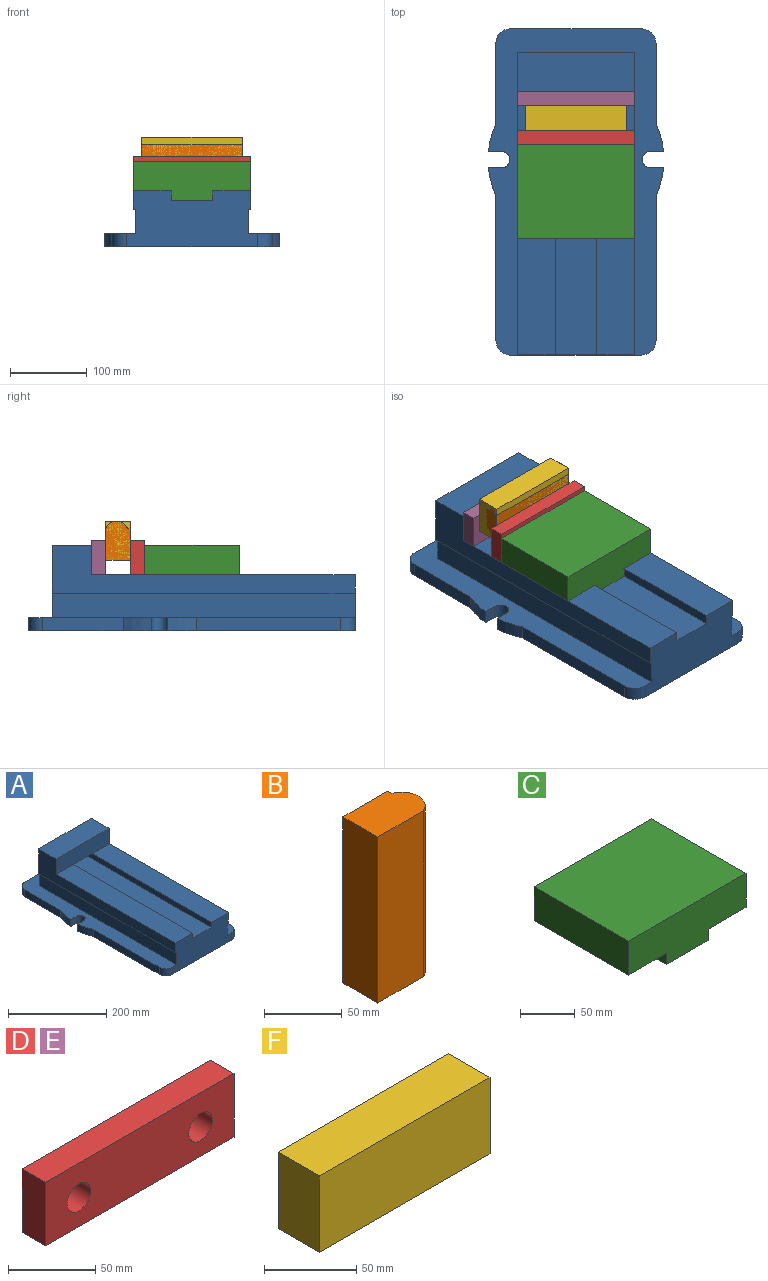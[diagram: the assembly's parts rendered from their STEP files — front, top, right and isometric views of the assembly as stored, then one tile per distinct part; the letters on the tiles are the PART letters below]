
ASSEMBLY  parts=6 mates=9
PART A: 37 faces, bbox 227.6x423.9x111.1 mm
  f0: plane 187.5x17.46mm, normal (1,0,0), area 3274.3mm2, adj f1,f18,f19,f21
  f1: cylinder r=114.3mm len=36.77mm, axis (0,0,-1), area 667.7mm2, adj f0,f2,f18,f21
  f2: plane 17.46x16.96mm, normal (0,1,0), area 296.2mm2, adj f1,f3,f18,f21
  f3: cylinder r=10.67mm len=21.35mm, axis (0,0,-1), area 585.5mm2, adj f2,f4,f18,f21
  f4: plane 17.46x16.96mm, normal (0,-1,0), area 296.2mm2, adj f3,f5,f18,f21
  f5: cylinder r=114.3mm len=36.77mm, axis (0,0,-1), area 667.7mm2, adj f4,f6,f18,f21
  f6: plane 103.37x17.46mm, normal (1,0,0), area 1805mm2, adj f5,f7,f18,f21
  f7: cylinder r=19.05mm len=19.05mm, axis (0,0,-1), area 522.5mm2, adj f6,f8,f18,f21
  f8: plane 171.12x17.46mm, normal (0,1,0), area 2988.2mm2, adj f7,f9,f18,f21
  f9: cylinder r=17.81mm len=17.81mm, axis (0,0,-1), area 488.4mm2, adj f8,f10,f18,f21
  f10: plane 104.61x17.46mm, normal (-1,0,0), area 1826.8mm2, adj f9,f11,f18,f21
  f11: cylinder r=114.3mm len=36.77mm, axis (0,0,-1), area 667.7mm2, adj f10,f12,f18,f21
  f12: plane 17.46x16.96mm, normal (0,-1,0), area 296.2mm2, adj f11,f13,f18,f21
  f13: cylinder r=10.67mm len=21.35mm, axis (0,0,-1), area 585.5mm2, adj f12,f14,f18,f21
  f14: plane 17.46x16.96mm, normal (0,1,0), area 296.2mm2, adj f13,f15,f18,f21
  f15: cylinder r=114.3mm len=36.77mm, axis (0,0,-1), area 667.7mm2, adj f14,f16,f18,f21
  f16: plane 187.5x17.46mm, normal (-1,0,0), area 3274.3mm2, adj f15,f17,f18,f21
  f17: cylinder r=19.05mm len=19.05mm, axis (0,0,-1), area 522.5mm2, adj f16,f18,f21,f27
  f18: plane 423.86x227.6mm, normal (0,0,-1), area 88071.8mm2, adj f0,f1,f2,f3,f4,f5,f6,f7
  f19: cylinder r=19.05mm len=19.05mm, axis (0,0,-1), area 522.5mm2, adj f0,f18,f21,f27
  f20: plane 393.7x31.75mm, normal (1,0,0), area 12500mm2, adj f21,f27,f28,f29
  f21: plane 423.86x227.6mm, normal (0,0,1), area 30572mm2, adj f0,f1,f2,f3,f4,f5,f6,f7
  f22: plane 393.7x31.75mm, normal (-1,0,0), area 12500mm2, adj f21,f24,f27,f29
  f23: plane 393.7x53.98mm, normal (0,0,1), area 21250mm2, adj f25,f26,f27,f29
  f24: plane 393.7x3.18mm, normal (0,0,-1), area 1250mm2, adj f22,f27,f29,f31
  f25: plane 393.7x12.7mm, normal (1,0,0), area 5000mm2, adj f23,f27,f29,f32,f33
  f26: plane 393.7x12.7mm, normal (-1,0,0), area 5000mm2, adj f23,f27,f29,f33,f34
  f27: plane 169.88x73.03mm, normal (0,-1,0), area 10547.1mm2, adj f17,f18,f19,f20,f21,f22,f23,f24
  f28: plane 393.7x3.18mm, normal (0,0,-1), area 1250mm2, adj f20,f27,f29,f35
  f29: plane 152.4x93.66mm, normal (0,1,0), area 13387.1mm2, adj f20,f21,f22,f23,f24,f25,f26,f28
  f30: plane 152.4x50.8mm, normal (0,0,1), area 7741.9mm2, adj f29,f31,f35,f36
  f31: plane 393.7x61.91mm, normal (-1,0,0), area 11310.5mm2, adj f24,f27,f29,f30,f32,f36
  f32: plane 342.9x49.21mm, normal (0,0,1), area 16875mm2, adj f25,f27,f31,f36
  f33: plane 53.98x50.8mm, normal (0,0,-1), area 2741.9mm2, adj f25,f26,f29,f36
  f34: plane 342.9x49.21mm, normal (0,0,1), area 16875mm2, adj f26,f27,f35,f36
  f35: plane 393.7x61.91mm, normal (1,0,0), area 11310.5mm2, adj f27,f28,f29,f30,f34,f36
  f36: plane 152.4x38.1mm, normal (0,-1,0), area 5806.4mm2, adj f30,f31,f32,f33,f34,f35
PART B: 7 faces, bbox 51x31.8x131 mm
  f0: plane 50.96x31.75mm, normal (0,0,1), area 1502mm2, adj f1,f2,f3,f4,f5
  f1: plane 130.96x3.81mm, normal (1,0,0), area 499mm2, adj f0,f2,f5,f6
  f2: plane 130.96x40.92mm, normal (0,1,0), area 5358.9mm2, adj f0,f1,f3,f6
  f3: plane 130.96x31.75mm, normal (-1,0,0), area 4158.1mm2, adj f0,f2,f4,f6
  f4: plane 130.96x41.58mm, normal (0,-1,0), area 5445.7mm2, adj f0,f3,f5,f6
  f5: cylinder r=15mm len=130.96mm, axis (0,0,1), area 4709.8mm2, adj f0,f1,f4,f6
  f6: plane 50.96x31.75mm, normal (0,0,-1), area 1502mm2, adj f1,f2,f3,f4,f5
PART C: 10 faces, bbox 152.4x122.2x50.8 mm
  f0: plane 152.4x122.24mm, normal (0,0,1), area 18629mm2, adj f1,f4,f6,f8
  f1: plane 122.24x38.1mm, normal (1,0,0), area 4657.2mm2, adj f0,f2,f6,f8
  f2: plane 122.24x49.21mm, normal (0,0,-1), area 6015.6mm2, adj f1,f3,f6,f8
  f3: plane 122.24x12.7mm, normal (1,0,0), area 1552.4mm2, adj f2,f5,f6,f8
  f4: plane 122.24x38.1mm, normal (-1,0,0), area 4657.2mm2, adj f0,f6,f7,f8
  f5: plane 122.24x53.98mm, normal (0,0,-1), area 6597.8mm2, adj f3,f6,f8,f9
  f6: plane 152.4x50.8mm, normal (0,-1,0), area 6491.9mm2, adj f0,f1,f2,f3,f4,f5,f7,f9
  f7: plane 122.24x49.21mm, normal (0,0,-1), area 6015.6mm2, adj f4,f6,f8,f9
  f8: plane 152.4x50.8mm, normal (0,1,0), area 6491.9mm2, adj f0,f1,f2,f3,f4,f5,f7,f9
  f9: plane 122.24x12.7mm, normal (-1,0,0), area 1552.4mm2, adj f5,f6,f7,f8
PART D: 8 faces, bbox 152.4x19.1x44.5 mm
  f0: cylinder r=9.53mm len=19.05mm, axis (0,1,0), area 1140.1mm2, adj f3,f5
  f1: cylinder r=9.53mm len=19.05mm, axis (0,1,0), area 1140.1mm2, adj f3,f5
  f2: plane 152.4x19.05mm, normal (0,0,1), area 2903.2mm2, adj f3,f4,f5,f6
  f3: plane 152.4x44.45mm, normal (0,1,0), area 6204.1mm2, adj f0,f1,f2,f4,f6,f7
  f4: plane 44.45x19.05mm, normal (1,0,0), area 846.8mm2, adj f2,f3,f5,f7
  f5: plane 152.4x44.45mm, normal (0,-1,0), area 6204.1mm2, adj f0,f1,f2,f4,f6,f7
  f6: plane 44.45x19.05mm, normal (-1,0,0), area 846.8mm2, adj f2,f3,f5,f7
  f7: plane 152.4x19.05mm, normal (0,0,-1), area 2903.2mm2, adj f3,f4,f5,f6
PART E: same geometry as D
PART F: 6 faces, bbox 131x31.8x50.8 mm
  f0: plane 130.96x31.75mm, normal (0,0,1), area 4158.1mm2, adj f1,f3,f4,f5
  f1: plane 130.96x50.8mm, normal (0,-1,0), area 6652.9mm2, adj f0,f2,f4,f5
  f2: plane 130.96x31.75mm, normal (0,0,-1), area 4158.1mm2, adj f1,f3,f4,f5
  f3: plane 130.96x50.8mm, normal (0,1,0), area 6652.9mm2, adj f0,f2,f4,f5
  f4: plane 50.8x31.75mm, normal (1,0,0), area 1612.9mm2, adj f0,f1,f2,f3
  f5: plane 50.8x31.75mm, normal (-1,0,0), area 1612.9mm2, adj f0,f1,f2,f3
PLACE A t=(0,-146.05,-61.91)mm
PLACE B rot(axis=(-0.71,0,-0.71),180deg) t=(0,-19.05,-19.05)mm
PLACE C t=(0,-69.85,-38.1)mm
PLACE D t=(0,-60.32,-38.1)mm
PLACE E rot(axis=(1,0,0),0deg) t=(0,-9.52,-38.1)mm
PLACE F rot(axis=(-1,0,0),0deg) t=(-65.48,-50.8,-21.2)mm
MATE planar A.f35 <-> D.f4  axis (1,0,0) through (76.2,-116.71,-44.71)mm
MATE planar D.f5 <-> C.f8  axis (0,-1,0) through (0,-69.85,-15.73)mm
MATE planar F.f1 <-> D.f3  axis (0,-1,0) through (0,-50.8,6.35)mm
MATE fastened F.f3 <-> B.f4  axis (0,1,0) through (0,-19.05,-19.05)mm
MATE planar D.f7 <-> A.f34  axis (0,0,-1) through (0,-60.32,-38.1)mm
MATE planar A.f32 <-> C.f7  axis (0,0,1) through (-51.59,-171.45,-38.1)mm
MATE fastened E.f5 <-> B.f4  axis (0,-1,0) through (0,-19.05,6.35)mm
MATE fastened E.f7 <-> A.f33  axis (0,0,1) through (0,0,-38.1)mm
MATE planar C.f3 <-> A.f26  axis (1,0,0) through (26.99,-130.97,-44.45)mm
